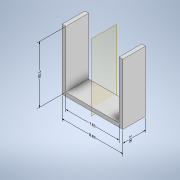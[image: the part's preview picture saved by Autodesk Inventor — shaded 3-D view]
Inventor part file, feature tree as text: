
AUTODESK INVENTOR PART (.ipt)
format: ipt  version: 2021 (Build 250183000, 183)  size: 121,856 bytes
history: native  units: in
note: dims shown in document units (in); Inventor stores cm internally (conversion verified against a paired STEP export)
features: other x5, extrude x1, mirror x1, sketch x1
ambient origin geometry x8: Origin, YZ Plane, XZ Plane, XY Plane, X Axis, Y Axis, Z Axis, Center Point
bodies: Solid1 (feature_tree)
feature tree (8):
  other  "Annotations"
  extrude  "Extrusion1"  Depth=8.0in
  mirror  "Mirror1"
  sketch  "Sketch3"  dims[d2=5.0in d6=8.0in d7=3.0in d8=0.0in d10=0.2318in d11=7.0in d12=0.3206in d13=0.2627in d14=8.0in d15=0.1954in d16=0.3027in d17=3.0in d18=0.0in d19=0.3937in d20=7.5in d9=0.1437in]
  other  "Linear Dimension 1"
  other  "Linear Dimension 2"
  other  "Linear Dimension 3"
  other  "Linear Dimension 4"
